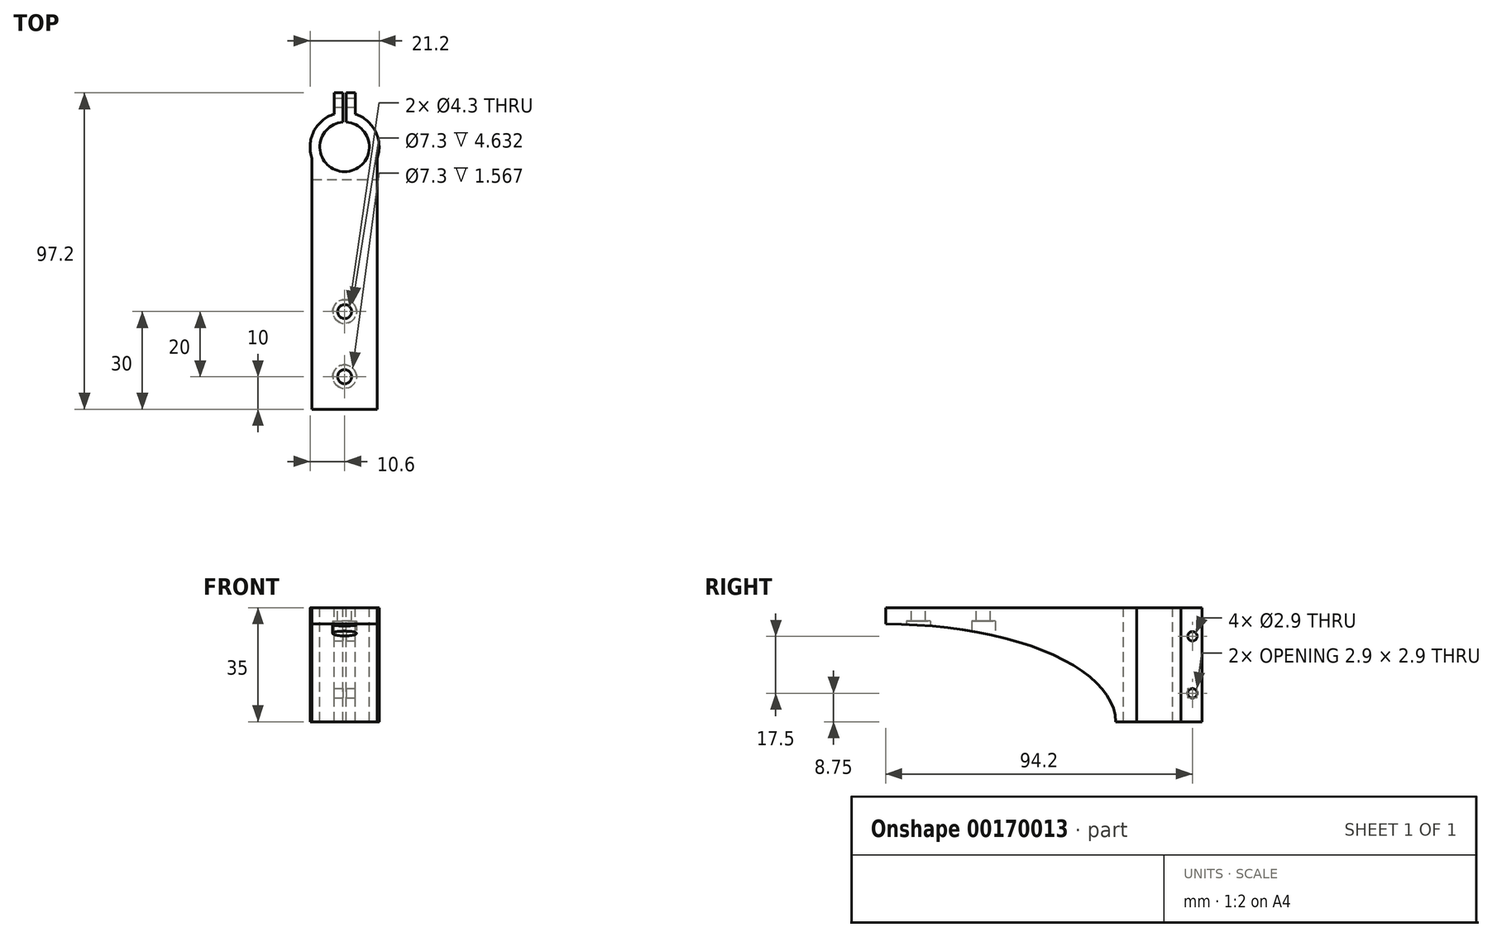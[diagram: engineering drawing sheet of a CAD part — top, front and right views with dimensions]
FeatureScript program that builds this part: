
annotation { "Feature Type Name" : "Feature", "Feature Type Description" : "" }
export const myFeature = defineFeature(function(context is Context, id is Id, definition is map)
    precondition{}
    {
        {
            var Q0;
            Q0=qCreatedBy(makeId("Top.planeOp"),FACE);
            var sketch = newSketch(context, id + "F0", { "sketchPlane" : qUnion([Q0])});
            skCircle(sketch, "E0", {"center": v(0, 0) * mm, "radius": 7.6 * mm});
            skArc(sketch, "E1.0", {"start": v(-3.25, 10.09) * mm, "mid": v(0, -10.6) * mm, "end": v(3.25, 10.09) * mm});
            skLineSegment(sketch, "E2.top", {"start": v(3.25, 16.6) * mm, "end": v(-3.25, 16.6) * mm});
            skLineSegment(sketch, "E2.left", {"start": v(3.25, 10.09) * mm, "end": v(3.25, 16.6) * mm});
            skLineSegment(sketch, "E2.right", {"start": v(-3.25, 10.09) * mm, "end": v(-3.25, 16.6) * mm});
            skPoint(sketch, "E2.middle", {"position": v(0, 10.6) * mm});
            skLineSegment(sketch, "E3.top", {"start": v(-10, -80.6) * mm, "end": v(10, -80.6) * mm});
            skLineSegment(sketch, "E3.left", {"start": v(-10, -3.52) * mm, "end": v(-10, -80.6) * mm});
            skLineSegment(sketch, "E3.right", {"start": v(10, -3.52) * mm, "end": v(10, -80.6) * mm});
            skSolve(sketch);
        }
        {
            var Q0;
            Q0=makeQuery(id+"F0.imprint","IMPRINT",FACE,{"disambiguationData":[TD([[makeQuery(id+"F0.imprint","IMPRINT",EDGE,{"derivedFrom":sQuery(id+"F0.wireOp",EDGE,"E3.top")}),1.0]])]});
            extrude(context, id + "F1", {"entities" : qUnion([Q0]), "oppositeDirection" : true, "depth" : 35 * mm});
        }
        {
            var Q0;
            Q0=makeQuery(id+"F0.imprint","IMPRINT",FACE,{"disambiguationData":[TD([[makeQuery(id+"F0.imprint","IMPRINT",EDGE,{"derivedFrom":sQuery(id+"F0.wireOp",EDGE,"E0")}),-1.0]])]});
            extrude(context, id + "F2", {"entities" : qUnion([Q0]), "operationType" : NewBodyOperationType.ADD, "oppositeDirection" : true, "depth" : 35 * mm});
        }
        {
            var Q0;
            {var subQ0=sQuery(id+"F0.wireOp",EDGE,"E1.0");Q0=makeQuery(id+"F2.boolean.opBoolean","MERGE",FACE,{"derivedFrom":[makeQuery(id+"F1.opExtrude","CAP_FACE",FACE,{"disambiguationData":[OSD([subQ0,sQuery(id+"F0.wireOp",EDGE,"E3.top"),sQuery(id+"F0.wireOp",EDGE,"E3.left"),sQuery(id+"F0.wireOp",EDGE,"E3.right")])],"isStart":true}),makeQuery(id+"F2.opExtrude","CAP_FACE",FACE,{"disambiguationData":[OSD([sQuery(id+"F0.wireOp",EDGE,"E0"),subQ0,sQuery(id+"F0.wireOp",EDGE,"E2.top"),sQuery(id+"F0.wireOp",EDGE,"E2.left"),sQuery(id+"F0.wireOp",EDGE,"E2.right")])],"isStart":true})]});}
            var sketch = newSketch(context, id + "F3", { "sketchPlane" : qUnion([Q0])});
            skCircle(sketch, "E4", {"center": v(0, -50.6) * mm, "radius": 2.15 * mm});
            skCircle(sketch, "E5", {"center": v(0, -70.6) * mm, "radius": 2.15 * mm});
            skSolve(sketch);
        }
        {
            var Q0;
            Q0 = qSketchRegion(id + "F3", true);
            extrude(context, id + "F4", {"entities" : qUnion([Q0]), "operationType" : NewBodyOperationType.REMOVE, "endBound" : BoundingType.THROUGH_ALL, "oppositeDirection" : true, "depth" : 25 * mm});
        }
        {
            var Q0;
            Q0=makeQuery(id+"F1.opExtrude","CAP_FACE",FACE,{"disambiguationData":[OSD([sQuery(id+"F0.wireOp",EDGE,"E0"),sQuery(id+"F0.wireOp",EDGE,"E1.0"),sQuery(id+"F0.wireOp",EDGE,"E2.top"),sQuery(id+"F0.wireOp",EDGE,"E2.left"),sQuery(id+"F0.wireOp",EDGE,"E2.right"),sQuery(id+"F0.wireOp",EDGE,"E3.top"),sQuery(id+"F0.wireOp",EDGE,"E3.left"),sQuery(id+"F0.wireOp",EDGE,"E3.right")])],"isStart":false});
            var sketch = newSketch(context, id + "F5", { "sketchPlane" : qUnion([Q0])});
            skCircle(sketch, "E6", {"center": v(0, 70.6) * mm, "radius": 3.65 * mm});
            skCircle(sketch, "E7", {"center": v(0, 50.6) * mm, "radius": 3.65 * mm});
            skSolve(sketch);
        }
        {
            var Q0;
            Q0=makeQuery(id+"F5.imprint","IMPRINT",FACE,{"disambiguationData":[TD([[makeQuery(id+"F5.imprint","IMPRINT",EDGE,{"derivedFrom":sQuery(id+"F5.wireOp",EDGE,"E6")}),1.0]])]});
            var Q1;
            Q1=makeQuery(id+"F5.imprint","IMPRINT",FACE,{"disambiguationData":[TD([[makeQuery(id+"F5.imprint","IMPRINT",EDGE,{"derivedFrom":sQuery(id+"F5.wireOp",EDGE,"E7")}),1.0]])]});
            extrude(context, id + "F6", {"entities" : qUnion([Q0, Q1]), "operationType" : NewBodyOperationType.REMOVE, "oppositeDirection" : true, "depth" : 31 * mm});
        }
        {
            var Q0;
            Q0=makeQuery(id+"F1.opExtrude","SWEPT_FACE",FACE,{"disambiguationData":[OSD([sQuery(id+"F0.wireOp",EDGE,"E3.right")])]});
            var sketch = newSketch(context, id + "F7", { "sketchPlane" : qUnion([Q0])});
            skLineSegment(sketch, "E8", {"start": v(-3.52, -35) * mm, "end": v(-10.02, -35) * mm});
            skLineSegment(sketch, "E9", {"start": v(-80.6, 0) * mm, "end": v(-80.6, -5) * mm});
            skEllipse(sketch, "E10", {"center": v(-80.6, -35) * mm, "majorRadius": 70.58 * mm, "minorRadius": 30 * mm, "majorAxis": v(1, 0)});
            skSolve(sketch);
        }
        {
            var Q0;
            {var subQ1=sQuery(id+"F0.wireOp",EDGE,"E3.right");var subQ2=makeQuery(id+"F1.opExtrude","SWEPT_EDGE",EDGE,{"disambiguationData":[OSD([sQuery(id+"F0.wireOp",EDGE,"E3.top"),subQ1])]});var subQ4=makeQuery(id+"F1.opExtrude","CAP_EDGE",EDGE,{"disambiguationData":[OSD([subQ1])],"isStart":false});var subQ6=makeQuery(id+"F7.imprint","INTERSECT",VERTEX,{"derivedFrom":[subQ2,subQ4]});Q0=makeQuery(id+"F7.imprint","IMPRINT",FACE,{"disambiguationData":[TD([[makeQuery(id+"F7.imprint","IMPRINT",EDGE,{"disambiguationData":[TD([[subQ6,1.0]])],"derivedFrom":subQ4}),-1.0]])]});}
            extrude(context, id + "F8", {"entities" : qUnion([Q0]), "operationType" : NewBodyOperationType.REMOVE, "endBound" : BoundingType.THROUGH_ALL, "oppositeDirection" : true, "depth" : 25 * mm});
        }
        {
            var Q0;
            Q0=makeQuery(id+"F1.opExtrude","CAP_FACE",FACE,{"disambiguationData":[OSD([sQuery(id+"F0.wireOp",EDGE,"E0"),sQuery(id+"F0.wireOp",EDGE,"E1.0"),sQuery(id+"F0.wireOp",EDGE,"E2.top"),sQuery(id+"F0.wireOp",EDGE,"E2.left"),sQuery(id+"F0.wireOp",EDGE,"E2.right"),sQuery(id+"F0.wireOp",EDGE,"E3.top"),sQuery(id+"F0.wireOp",EDGE,"E3.left"),sQuery(id+"F0.wireOp",EDGE,"E3.right")])],"isStart":true});
            var sketch = newSketch(context, id + "F9", { "sketchPlane" : qUnion([Q0])});
            skLineSegment(sketch, "E11.bottom", {"start": v(0, 18.6) * mm, "end": v(-0.5, 18.6) * mm});
            skLineSegment(sketch, "E11.top", {"start": v(0, 0) * mm, "end": v(-0.5, 0) * mm});
            skLineSegment(sketch, "E11.left", {"start": v(0, 18.6) * mm, "end": v(0, 0) * mm});
            skLineSegment(sketch, "E11.right", {"start": v(-0.5, 18.6) * mm, "end": v(-0.5, 0) * mm});
            skLineSegment(sketch, "E12.MirrorCS", {"start": v(0.5, 18.6) * mm, "end": v(0.5, 0) * mm});
            skLineSegment(sketch, "E13.MirrorCS", {"start": v(0, 0) * mm, "end": v(0.5, 0) * mm});
            skLineSegment(sketch, "E14.MirrorCS", {"start": v(0, 18.6) * mm, "end": v(0.5, 18.6) * mm});
            skSolve(sketch);
        }
        {
            var Q0;
            {var subQ0=sQuery(id+"F9.wireOp",EDGE,"E11.left");var subQ1=makeQuery(id+"F2.opExtrude","CAP_EDGE",EDGE,{"disambiguationData":[OSD([sQuery(id+"F0.wireOp",EDGE,"E2.top")])],"isStart":true});var subQ2=makeQuery(id+"F9.imprint","INTERSECT",VERTEX,{"derivedFrom":[subQ1,subQ0]});Q0=makeQuery(id+"F9.imprint","IMPRINT",FACE,{"disambiguationData":[TD([[makeQuery(id+"F9.imprint","IMPRINT",EDGE,{"disambiguationData":[TD([[subQ2,-1.0]])],"derivedFrom":subQ0}),1.0]])]});}
            var Q1;
            {var subQ0=sQuery(id+"F9.wireOp",EDGE,"E11.top");Q1=makeQuery(id+"F9.imprint","IMPRINT",FACE,{"disambiguationData":[TD([[makeQuery(id+"F9.imprint","IMPRINT",EDGE,{"derivedFrom":subQ0}),-1.0]])]});}
            var Q2;
            {var subQ0=sQuery(id+"F9.wireOp",EDGE,"E11.bottom");Q2=makeQuery(id+"F9.imprint","IMPRINT",FACE,{"disambiguationData":[TD([[makeQuery(id+"F9.imprint","IMPRINT",EDGE,{"derivedFrom":subQ0}),1.0]])]});}
            var Q3;
            {var subQ0=sQuery(id+"F9.wireOp",EDGE,"E14.MirrorCS");Q3=makeQuery(id+"F9.imprint","IMPRINT",FACE,{"disambiguationData":[TD([[makeQuery(id+"F9.imprint","IMPRINT",EDGE,{"derivedFrom":subQ0}),-1.0]])]});}
            var Q4;
            {var subQ0=sQuery(id+"F9.wireOp",EDGE,"E13.MirrorCS");Q4=makeQuery(id+"F9.imprint","IMPRINT",FACE,{"disambiguationData":[TD([[makeQuery(id+"F9.imprint","IMPRINT",EDGE,{"derivedFrom":subQ0}),1.0]])]});}
            var Q5;
            {var subQ0=sQuery(id+"F9.wireOp",EDGE,"E11.left");var subQ1=makeQuery(id+"F2.opExtrude","CAP_EDGE",EDGE,{"disambiguationData":[OSD([sQuery(id+"F0.wireOp",EDGE,"E2.top")])],"isStart":true});var subQ2=makeQuery(id+"F9.imprint","INTERSECT",VERTEX,{"derivedFrom":[subQ1,subQ0]});Q5=makeQuery(id+"F9.imprint","IMPRINT",FACE,{"disambiguationData":[TD([[makeQuery(id+"F9.imprint","IMPRINT",EDGE,{"disambiguationData":[TD([[subQ2,-1.0]])],"derivedFrom":subQ0}),-1.0]])]});}
            extrude(context, id + "F10", {"entities" : qUnion([Q0, Q1, Q2, Q3, Q4, Q5]), "operationType" : NewBodyOperationType.REMOVE, "endBound" : BoundingType.THROUGH_ALL, "oppositeDirection" : true, "depth" : 25 * mm});
        }
        {
            var Q0;
            Q0=makeQuery(id+"F2.opExtrude","SWEPT_FACE",FACE,{"disambiguationData":[OSD([sQuery(id+"F0.wireOp",EDGE,"E2.left")])]});
            var sketch = newSketch(context, id + "F11", { "sketchPlane" : qUnion([Q0])});
            skCircle(sketch, "E15", {"center": v(13.6, -8.75) * mm, "radius": 1.45 * mm});
            skCircle(sketch, "E16", {"center": v(13.6, -26.25) * mm, "radius": 1.45 * mm});
            skCircle(sketch, "E17.0", {"center": v(13.6, -8.75) * mm, "radius": 2.45 * mm});
            skCircle(sketch, "E18.0", {"center": v(13.6, -26.25) * mm, "radius": 2.45 * mm});
            skSolve(sketch);
        }
        {
            var Q0;
            Q0=makeQuery(id+"F11.imprint","IMPRINT",FACE,{"disambiguationData":[TD([[makeQuery(id+"F11.imprint","IMPRINT",EDGE,{"derivedFrom":sQuery(id+"F11.wireOp",EDGE,"E15")}),1.0]])]});
            var Q1;
            Q1=makeQuery(id+"F11.imprint","IMPRINT",FACE,{"disambiguationData":[TD([[makeQuery(id+"F11.imprint","IMPRINT",EDGE,{"derivedFrom":sQuery(id+"F11.wireOp",EDGE,"E16")}),1.0]])]});
            extrude(context, id + "F12", {"entities" : qUnion([Q0, Q1]), "operationType" : NewBodyOperationType.REMOVE, "endBound" : BoundingType.THROUGH_ALL, "oppositeDirection" : true, "depth" : 25 * mm});
        }
    });
